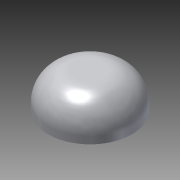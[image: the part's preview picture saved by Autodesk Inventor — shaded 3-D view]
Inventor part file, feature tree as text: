
AUTODESK INVENTOR PART (.ipt)
format: ipt  version: 2015 (Build 190159000, 159)  size: 104,448 bytes
history: native  units: in
note: dims shown in document units (in); Inventor stores cm internally (conversion verified against a paired STEP export)
features: extrude x1, fillet x1, sketch x1
ambient origin geometry x8: Origin, YZ Plane, XZ Plane, XY Plane, X Axis, Y Axis, Z Axis, Center Point
bodies: Solid1 (feature_tree)
feature tree (3):
  extrude  "Extrusion1"  Depth=0.125in TaperAngle=0.0deg
  fillet  "Fillet1"  Radius=0.1in
  sketch  "Sketch1"  dims[d0=0.3in d1=0.125in d2=0.0in d3=0.1in]
